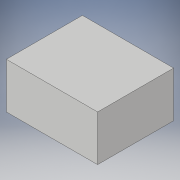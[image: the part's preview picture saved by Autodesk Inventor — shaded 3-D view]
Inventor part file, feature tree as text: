
AUTODESK INVENTOR PART (.ipt)
format: ipt  version: 2018 (Build 220112000, 112)  size: 84,992 bytes
history: native  units: in
note: dims shown in document units (in); Inventor stores cm internally (conversion verified against a paired STEP export)
features: extrude x1, sketch x1
ambient origin geometry x8: Origin, YZ Plane, XZ Plane, XY Plane, X Axis, Y Axis, Z Axis, Center Point
bodies: Solid1 (feature_tree)
feature tree (2):
  extrude  "Extrusion1"  Depth=0.2953in
  sketch  "Sketch1"  dims[d0=0.3543in d1=0.2953in d2=0.1772in d3=0.0in]
